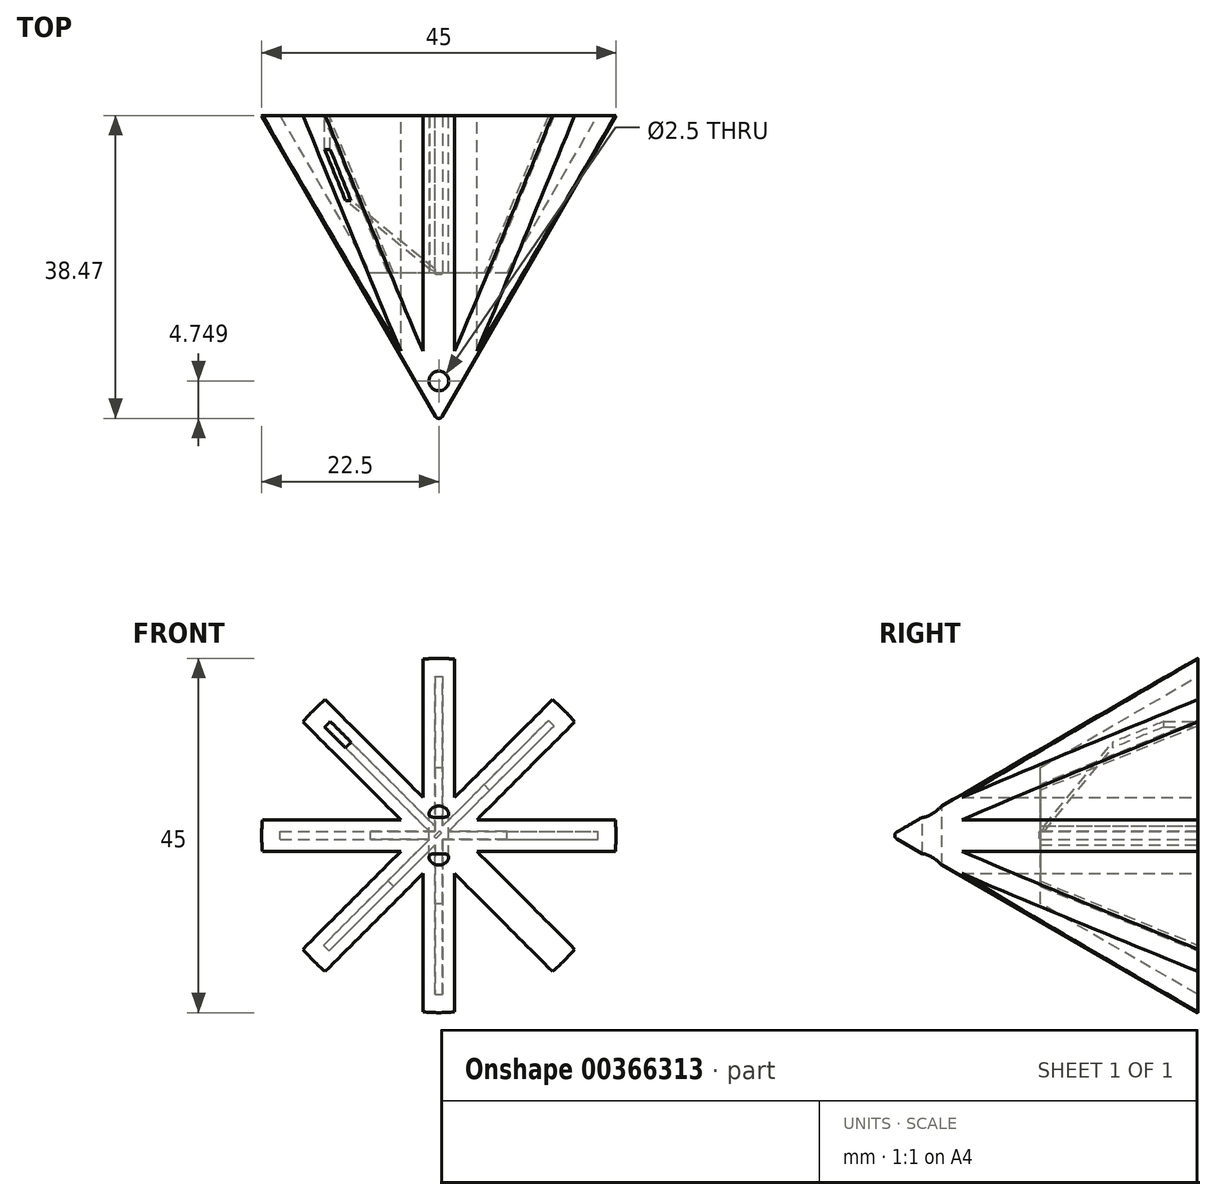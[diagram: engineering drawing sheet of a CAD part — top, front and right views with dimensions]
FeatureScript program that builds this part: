
annotation { "Feature Type Name" : "Feature", "Feature Type Description" : "" }
export const myFeature = defineFeature(function(context is Context, id is Id, definition is map)
    precondition{}
    {
        {
            var Q0;
            Q0=qCreatedBy(makeId("Front.planeOp"),FACE);
            var sketch = newSketch(context, id + "F0", { "sketchPlane" : qUnion([Q0])});
            skCircle(sketch, "E0.cCircle", {"center": v(0, 0) * mm, "radius": 20.79 * mm, "construction": true});
            skLineSegment(sketch, "E0.0", {"start": v(-22.5, 0) * mm, "end": v(-15.9, 15.9) * mm});
            skLineSegment(sketch, "E0.1", {"start": v(-15.9, 15.9) * mm, "end": v(0, 22.5) * mm});
            skLineSegment(sketch, "E0.2", {"start": v(0, 22.5) * mm, "end": v(15.9, 15.9) * mm});
            skLineSegment(sketch, "E0.3", {"start": v(15.9, 15.9) * mm, "end": v(22.5, 0) * mm});
            skLineSegment(sketch, "E0.4", {"start": v(22.5, 0) * mm, "end": v(15.9, -15.9) * mm});
            skLineSegment(sketch, "E0.5", {"start": v(15.9, -15.9) * mm, "end": v(0, -22.5) * mm});
            skLineSegment(sketch, "E0.6", {"start": v(0, -22.5) * mm, "end": v(-15.9, -15.9) * mm});
            skLineSegment(sketch, "E0.7", {"start": v(-15.9, -15.9) * mm, "end": v(-22.5, 0) * mm});
            skLineSegment(sketch, "E1", {"start": v(0, 22.5) * mm, "end": v(0, -22.5) * mm});
            skLineSegment(sketch, "E2", {"start": v(-15.9, -15.9) * mm, "end": v(15.9, 15.9) * mm});
            skLineSegment(sketch, "E3", {"start": v(-15.9, 15.9) * mm, "end": v(15.9, -15.9) * mm});
            skLineSegment(sketch, "E4", {"start": v(22.5, 0) * mm, "end": v(-22.5, 0) * mm});
            skSolve(sketch);
        }
        {
            var Q0;
            Q0=qCreatedBy(makeId("Top.planeOp"),FACE);
            var sketch = newSketch(context, id + "F1", { "sketchPlane" : qUnion([Q0])});
            skLineSegment(sketch, "E5", {"start": v(-22.5, 0) * mm, "end": v(0, -38.97) * mm});
            skLineSegment(sketch, "E6", {"start": v(0, -38.97) * mm, "end": v(22.5, 0) * mm});
            skLineSegment(sketch, "E7", {"start": v(22.5, 0) * mm, "end": v(-22.5, 0) * mm});
            skLineSegment(sketch, "E8", {"start": v(0, -69.99) * mm, "end": v(0, 32.44) * mm, "construction": true});
            skSolve(sketch);
        }
        {
            var Q0;
            Q0=makeQuery(id+"F1.imprint","IMPRINT",FACE,{"disambiguationData":[TD([[makeQuery(id+"F1.imprint","IMPRINT",EDGE,{"derivedFrom":sQuery(id+"F1.wireOp",EDGE,"E5")}),1.0]])]});
            extrude(context, id + "F2", {"entities" : qUnion([Q0]), "depth" : 2 * mm, "hasSecondDirection" : true, "secondDirectionOppositeDirection" : true, "secondDirectionDepth" : 2 * mm});
        }
        {
            var Q0;
            Q0=makeQuery(id+"F2.opExtrude","SWEPT_BODY",BODY,{"disambiguationData":[OSD([sQuery(id+"F1.wireOp",EDGE,"E5"),sQuery(id+"F1.wireOp",EDGE,"E6"),sQuery(id+"F1.wireOp",EDGE,"E7")])]});
            var Q1;
            Q1=sQuery(id+"F1.wireOp",EDGE,"E8");
            transform(context, id + "F3", {"entities" : qUnion([Q0]), "transformType" : TransformType.ROTATION, "transformAxis" : qUnion([Q1]), "angle" : 45 * degree, "makeCopy" : true});
        }
        {
            var Q0;
            Q0=makeQuery(id+"F3.opPattern","COPY",BODY,{"derivedFrom":makeQuery(id+"F2.opExtrude","SWEPT_BODY",BODY,{"disambiguationData":[OSD([sQuery(id+"F1.wireOp",EDGE,"E5"),sQuery(id+"F1.wireOp",EDGE,"E6"),sQuery(id+"F1.wireOp",EDGE,"E7")])]}),"instanceName":"1"});
            var Q1;
            Q1=sQuery(id+"F1.wireOp",EDGE,"E8");
            transform(context, id + "F4", {"entities" : qUnion([Q0]), "transformType" : TransformType.ROTATION, "transformAxis" : qUnion([Q1]), "angle" : 45 * degree, "makeCopy" : true});
        }
        {
            var Q0;
            Q0=makeQuery(id+"F4.opPattern","COPY",BODY,{"derivedFrom":makeQuery(id+"F3.opPattern","COPY",BODY,{"derivedFrom":makeQuery(id+"F2.opExtrude","SWEPT_BODY",BODY,{"disambiguationData":[OSD([sQuery(id+"F1.wireOp",EDGE,"E5"),sQuery(id+"F1.wireOp",EDGE,"E6"),sQuery(id+"F1.wireOp",EDGE,"E7")])]}),"instanceName":"1"}),"instanceName":"1"});
            var Q1;
            Q1=sQuery(id+"F1.wireOp",EDGE,"E8");
            transform(context, id + "F5", {"entities" : qUnion([Q0]), "transformType" : TransformType.ROTATION, "transformAxis" : qUnion([Q1]), "angle" : 45 * degree, "makeCopy" : true});
        }
        {
            var Q0;
            Q0=makeQuery(id+"F2.opExtrude","SWEPT_BODY",BODY,{"disambiguationData":[OSD([sQuery(id+"F1.wireOp",EDGE,"E5"),sQuery(id+"F1.wireOp",EDGE,"E6"),sQuery(id+"F1.wireOp",EDGE,"E7")])]});
            var Q1;
            Q1=makeQuery(id+"F3.opPattern","COPY",BODY,{"derivedFrom":makeQuery(id+"F2.opExtrude","SWEPT_BODY",BODY,{"disambiguationData":[OSD([sQuery(id+"F1.wireOp",EDGE,"E5"),sQuery(id+"F1.wireOp",EDGE,"E6"),sQuery(id+"F1.wireOp",EDGE,"E7")])]}),"instanceName":"1"});
            var Q2;
            Q2=makeQuery(id+"F4.opPattern","COPY",BODY,{"derivedFrom":makeQuery(id+"F3.opPattern","COPY",BODY,{"derivedFrom":makeQuery(id+"F2.opExtrude","SWEPT_BODY",BODY,{"disambiguationData":[OSD([sQuery(id+"F1.wireOp",EDGE,"E5"),sQuery(id+"F1.wireOp",EDGE,"E6"),sQuery(id+"F1.wireOp",EDGE,"E7")])]}),"instanceName":"1"}),"instanceName":"1"});
            var Q3;
            Q3=makeQuery(id+"F5.opPattern","COPY",BODY,{"derivedFrom":makeQuery(id+"F4.opPattern","COPY",BODY,{"derivedFrom":makeQuery(id+"F3.opPattern","COPY",BODY,{"derivedFrom":makeQuery(id+"F2.opExtrude","SWEPT_BODY",BODY,{"disambiguationData":[OSD([sQuery(id+"F1.wireOp",EDGE,"E5"),sQuery(id+"F1.wireOp",EDGE,"E6"),sQuery(id+"F1.wireOp",EDGE,"E7")])]}),"instanceName":"1"}),"instanceName":"1"}),"instanceName":"1"});
            booleanBodies(context, id + "F6", {"operationType" : BooleanOperationType.UNION, "tools" : qUnion([Q0, Q1, Q2, Q3])});
        }
        {
            var Q0;
            Q0=qCreatedBy(makeId("Right.planeOp"),FACE);
            var Q1;
            Q1=sQuery(id+"F1.wireOp",EDGE,"E8");
            cPlane(context, id + "F7", {"entities" : qUnion([Q0, Q1]), "cplaneType" : CPlaneType.LINE_ANGLE, "offset" : 25 * mm, "angle" : 45 * degree, "width" : 150 * mm, "height" : 150 * mm});
        }
        {
            var Q0;
            Q0=qCreatedBy(makeId("Top.planeOp"),FACE);
            var Q1;
            Q1=sQuery(id+"F1.wireOp",EDGE,"E8");
            cPlane(context, id + "F8", {"entities" : qUnion([Q0, Q1]), "cplaneType" : CPlaneType.LINE_ANGLE, "offset" : 25 * mm, "angle" : 45 * degree, "width" : 150 * mm, "height" : 150 * mm});
        }
        {
            var Q0;
            Q0=qCreatedBy(id+"F7.planeOp",FACE);
            var sketch = newSketch(context, id + "F9", { "sketchPlane" : qUnion([Q0])});
            skLineSegment(sketch, "E9", {"start": v(20, -8.64) * mm, "end": v(0, -20.2) * mm});
            skLineSegment(sketch, "E10", {"start": v(0, -20.2) * mm, "end": v(0, 20.2) * mm});
            skLineSegment(sketch, "E11", {"start": v(0, 20.2) * mm, "end": v(20, 8.64) * mm});
            skLineSegment(sketch, "E12", {"start": v(20, 8.64) * mm, "end": v(20, -8.64) * mm});
            skPoint(sketch, "E13.orphan", {"position": v(34.97, 0) * mm});
            skSolve(sketch);
        }
        {
            var Q0;
            Q0=qSketchRegion(id+"F9",true);
            extrude(context, id + "F10", {"entities" : qUnion([Q0]), "operationType" : NewBodyOperationType.REMOVE, "endBound" : BoundingType.SYMMETRIC, "oppositeDirection" : true, "depth" : 1 * mm});
        }
        {
            var Q0;
            Q0=qCreatedBy(makeId("Right.planeOp"),FACE);
            var sketch = newSketch(context, id + "F11", { "sketchPlane" : qUnion([Q0])});
            skLineSegment(sketch, "E14", {"start": v(0, -20.2) * mm, "end": v(-20, -8.64) * mm});
            skLineSegment(sketch, "E15", {"start": v(-20, 8.64) * mm, "end": v(0, 20.2) * mm});
            skLineSegment(sketch, "E16", {"start": v(0, 20.2) * mm, "end": v(0, -20.2) * mm});
            skLineSegment(sketch, "E17", {"start": v(-20, -8.64) * mm, "end": v(-20, 8.64) * mm});
            skPoint(sketch, "E18.orphan", {"position": v(-34.97, 0) * mm});
            skSolve(sketch);
        }
        {
            var Q0;
            Q0=qSketchRegion(id+"F11",true);
            extrude(context, id + "F12", {"entities" : qUnion([Q0]), "operationType" : NewBodyOperationType.REMOVE, "endBound" : BoundingType.SYMMETRIC, "oppositeDirection" : true, "depth" : 1 * mm});
        }
        {
            var Q0;
            Q0=qCreatedBy(id+"F8.planeOp",FACE);
            var sketch = newSketch(context, id + "F13", { "sketchPlane" : qUnion([Q0])});
            skLineSegment(sketch, "E19", {"start": v(20.2, 0) * mm, "end": v(8.64, 20) * mm});
            skLineSegment(sketch, "E20", {"start": v(-8.64, 20) * mm, "end": v(-20.2, 0) * mm});
            skLineSegment(sketch, "E21", {"start": v(-20.2, 0) * mm, "end": v(20.2, 0) * mm});
            skLineSegment(sketch, "E22", {"start": v(8.64, 20) * mm, "end": v(-8.64, 20) * mm});
            skPoint(sketch, "E23.orphan", {"position": v(0, 34.97) * mm});
            skSolve(sketch);
        }
        {
            var Q0;
            Q0=qCreatedBy(makeId("Top.planeOp"),FACE);
            var sketch = newSketch(context, id + "F14", { "sketchPlane" : qUnion([Q0])});
            skLineSegment(sketch, "E24.0", {"start": v(-20.2, 0) * mm, "end": v(-8.64, -20) * mm});
            skLineSegment(sketch, "E24.2", {"start": v(8.64, -20) * mm, "end": v(20.2, 0) * mm});
            skLineSegment(sketch, "E25", {"start": v(-20.2, 0) * mm, "end": v(20.2, 0) * mm});
            skLineSegment(sketch, "E26", {"start": v(8.64, -20) * mm, "end": v(-8.64, -20) * mm});
            skSolve(sketch);
        }
        {
            var Q0;
            Q0=qSketchRegion(id+"F14",true);
            extrude(context, id + "F15", {"entities" : qUnion([Q0]), "operationType" : NewBodyOperationType.REMOVE, "endBound" : BoundingType.SYMMETRIC, "oppositeDirection" : true, "depth" : 1 * mm});
        }
        {
            var Q0;
            Q0=qCreatedBy(makeId("Top.planeOp"),FACE);
            var sketch = newSketch(context, id + "F16", { "sketchPlane" : qUnion([Q0])});
            skLineSegment(sketch, "E27", {"start": v(22.5, 0) * mm, "end": v(0.43, -38.22) * mm});
            skLineSegment(sketch, "E28", {"start": v(0, -40.97) * mm, "end": v(49.3, -40.97) * mm});
            skLineSegment(sketch, "E29", {"start": v(0, -38.97) * mm, "end": v(0, -40.97) * mm});
            skLineSegment(sketch, "E30", {"start": v(22.5, 0) * mm, "end": v(47.75, 0) * mm});
            skLineSegment(sketch, "E31", {"start": v(47.75, 0) * mm, "end": v(49.3, -40.97) * mm});
            skArc(sketch, "E32", {"start": v(0, -38.47) * mm, "mid": v(0.25, -38.4) * mm, "end": v(0.43, -38.22) * mm});
            skLineSegment(sketch, "E33", {"start": v(0, -38.47) * mm, "end": v(0, -38.97) * mm});
            skSolve(sketch);
        }
        {
            var Q0;
            Q0=makeQuery(id+"F16.imprint","IMPRINT",FACE,{"disambiguationData":[TD([[makeQuery(id+"F16.imprint","IMPRINT",EDGE,{"derivedFrom":sQuery(id+"F16.wireOp",EDGE,"E27")}),1.0]])]});
            var Q1;
            Q1=sQuery(id+"F1.wireOp",EDGE,"E8");
            revolve(context, id + "F17", {"operationType" : NewBodyOperationType.REMOVE, "entities" : qUnion([Q0]), "axis" : qUnion([Q1]), "revolveType" : RevolveType.FULL, "oppositeDirection" : true});
        }
        {
            var Q0;
            Q0=qSketchRegion(id+"F13",true);
            extrude(context, id + "F18", {"entities" : qUnion([Q0]), "operationType" : NewBodyOperationType.REMOVE, "endBound" : BoundingType.SYMMETRIC, "oppositeDirection" : true, "depth" : 1 * mm});
        }
        {
            var Q0;
            Q0=qCreatedBy(makeId("Top.planeOp"),FACE);
            var sketch = newSketch(context, id + "F19", { "sketchPlane" : qUnion([Q0])});
            skCircle(sketch, "E34", {"center": v(0, -33.72) * mm, "radius": 1.25 * mm});
            skSolve(sketch);
        }
        {
            var Q0;
            Q0 = qSketchRegion(id + "F19", true);
            extrude(context, id + "F20", {"entities" : qUnion([Q0]), "operationType" : NewBodyOperationType.REMOVE, "endBound" : BoundingType.THROUGH_ALL, "oppositeDirection" : true, "depth" : 25 * mm, "hasSecondDirection" : true, "secondDirectionBound" : SecondDirectionBoundingType.THROUGH_ALL, "secondDirectionOppositeDirection" : false, "secondDirectionDepth" : 25 * mm});
        }
    });
